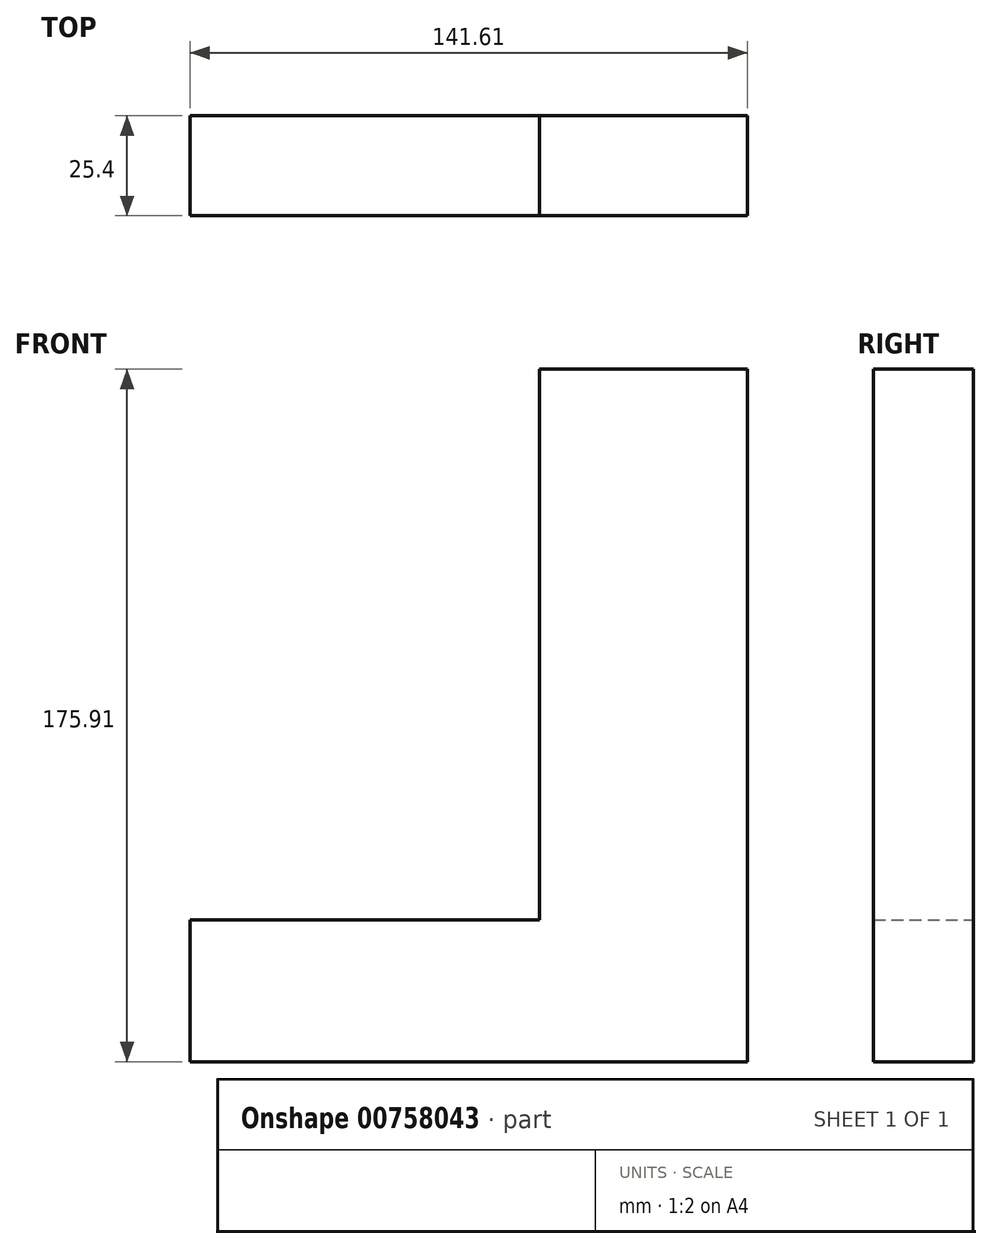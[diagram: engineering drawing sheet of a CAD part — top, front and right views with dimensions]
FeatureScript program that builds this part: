
annotation { "Feature Type Name" : "Feature", "Feature Type Description" : "" }
export const myFeature = defineFeature(function(context is Context, id is Id, definition is map)
    precondition{}
    {
        {
            var Q0;
            Q0=qCreatedBy(makeId("Front.planeOp"),FACE);
            var sketch = newSketch(context, id + "F0", { "sketchPlane" : qUnion([Q0])});
            skLineSegment(sketch, "E0.bottom", {"start": v(61.25, -175.91) * mm, "end": v(-183.76, -175.91) * mm});
            skLineSegment(sketch, "E0.top", {"start": v(61.25, 78.09) * mm, "end": v(-183.76, 78.09) * mm});
            skLineSegment(sketch, "E0.left", {"start": v(61.25, -175.91) * mm, "end": v(61.25, 78.09) * mm});
            skLineSegment(sketch, "E0.right", {"start": v(-183.76, -175.91) * mm, "end": v(-183.76, 78.09) * mm});
            skPoint(sketch, "E0.middle", {"position": v(-61.25, -48.91) * mm});
            skLineSegment(sketch, "E1", {"start": v(61.25, -175.91) * mm, "end": v(202.86, -175.91) * mm});
            skLineSegment(sketch, "E2", {"start": v(202.86, -175.91) * mm, "end": v(202.86, 0) * mm});
            skLineSegment(sketch, "E3", {"start": v(61.25, -139.95) * mm, "end": v(150.04, -139.95) * mm});
            skLineSegment(sketch, "E4", {"start": v(150.04, -139.95) * mm, "end": v(150.04, 0) * mm});
            skLineSegment(sketch, "E5", {"start": v(150.04, 0) * mm, "end": v(202.86, 0) * mm});
            skSolve(sketch);
        }
        {
            var Q0;
            {var subQ0=sQuery(id+"F0.wireOp",EDGE,"E1");Q0=makeQuery(id+"F0.imprint","IMPRINT",FACE,{"disambiguationData":[TD([[makeQuery(id+"F0.imprint","IMPRINT",EDGE,{"derivedFrom":subQ0}),1.0]])]});}
            extrude(context, id + "F1", {"entities" : qUnion([Q0]), "endBound" : BoundingType.SYMMETRIC, "depth" : 25.4 * mm, "offsetDistance" : 25.4 * mm, "hasSecondDirection" : true, "secondDirectionOppositeDirection" : true, "secondDirectionDepth" : 25.4 * mm});
        }
    });
